# Revit family: Toilet_Seat-Elongated_Closed_Front-KOHLER-C3-050-K-18751T_1
name_source: partatom
category: Specialty Equipment
revit_build: Autodesk Revit 2017 (Build: 20160225_1515(x64)
units: mm (PartAtom-declared; Revit-internal decimal feet)

## family parameters
Cut with Voids When Loaded = No
Host = Face
OmniClass Number = 23.31.25.00
OmniClass Title = Toilet and Bath Specialties
Part Type = Normal
Room Calculation Point = No
Round Connector Dimension = Use Diameter
Shared = No

## types (1)
- 0-White
    ADA Compliant = No
    Apparent Load = 2200 VA
    Assembly Code = C1030200
    CW Connection = Yes
    Cold Water Inlet = Cold Water Inlet
    Date Modified = 12/22/2020
    Default Elevation = 0"
    Description = Qingshubao Smart Toilet Cover
    Electrical Connector = Yes
    Electrical Note = One dedicated circuit required, protected with Class A Ground-Fault Circuit-Interrupter (GFCI) or Residual Current Device (RCD)
    Finish = Kohler-Plastic-0-White
    Height = 4 3/4"
    Length = 20 11/16"
    Manufacturer = KOHLER Co.
    MasterFormat 1995 = 10820
    MasterFormat 2004 = 10.28.13
    Material = Polypropylene Plastic
    Model = K-18751T-0
    Product Documentation Link = https://files.kohler.com.cn
    Product Name = C3-050
    Product Page URL = https://www.kohler.com.cn
    URL = http://www.kohler.com.cn
    Voltage = 220 V
    Width = 16 15/16"

## geometry (parser evidence)
native form markers: Sweep x5
no freeform markers — native parametric forms only
